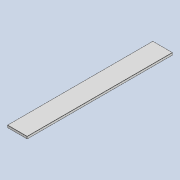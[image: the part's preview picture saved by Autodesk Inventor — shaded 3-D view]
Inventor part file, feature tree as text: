
AUTODESK INVENTOR PART (.ipt)
format: ipt  version: 2021 (Build 250183000, 183)  size: 142,336 bytes
history: native  units: mm
features: other x19, sketch x5
ambient origin geometry x8: Origin, YZ Plane, XZ Plane, XY Plane, X Axis, Y Axis, Z Axis, Center Point
bodies: Body1 (feature_tree)
feature tree (24):
  other  "Sólido1"
  other  "Cara1"
  other  "Pestaña1"
  other  "Pestaña2"
  other  "Pestaña3"
  other  "Pestaña4"
  sketch  "Boceto1"  dims[d0=900.0mm]
  other  "Placa1"
  sketch  "Boceto2"  dims[d1=6600.0mm]
  other  "Placa2"
  other  "Doblez1"
  other  "Esquina1"
  sketch  "Boceto3"  dims[d2=4.572mm]
  other  "Placa3"
  other  "Doblez2"
  other  "Esquina2"
  sketch  "Boceto4"  dims[d3=4.572mm]
  other  "Placa4"
  other  "Doblez3"
  other  "Esquina3"
  sketch  "Boceto5"  dims[d4=2.286mm d5=9.144mm d6=4.572mm d7=100.0mm d8=90.0deg d9=4.572mm d10=18.288mm d11=4.572mm d12=4.572mm d13=4.572mm d14=2.286mm d15=9.144mm d16=4.572mm d17=100.0mm d18=90.0deg d19=4.572mm d20=18.288mm d21=4.572mm d22=4.572mm d23=4.572mm d24=2.286mm d25=9.144mm d26=4.572mm d27=100.0mm d28=90.0deg d29=4.572mm d30=18.288mm d31=4.572mm d32=4.572mm d33=4.572mm d34=2.286mm d35=9.144mm d36=4.572mm d37=100.0mm d38=90.0deg d39=4.572mm d40=18.288mm d41=4.572mm d42=4.572mm]
  other  "Placa5"
  other  "Doblez4"
  other  "Esquina4"
